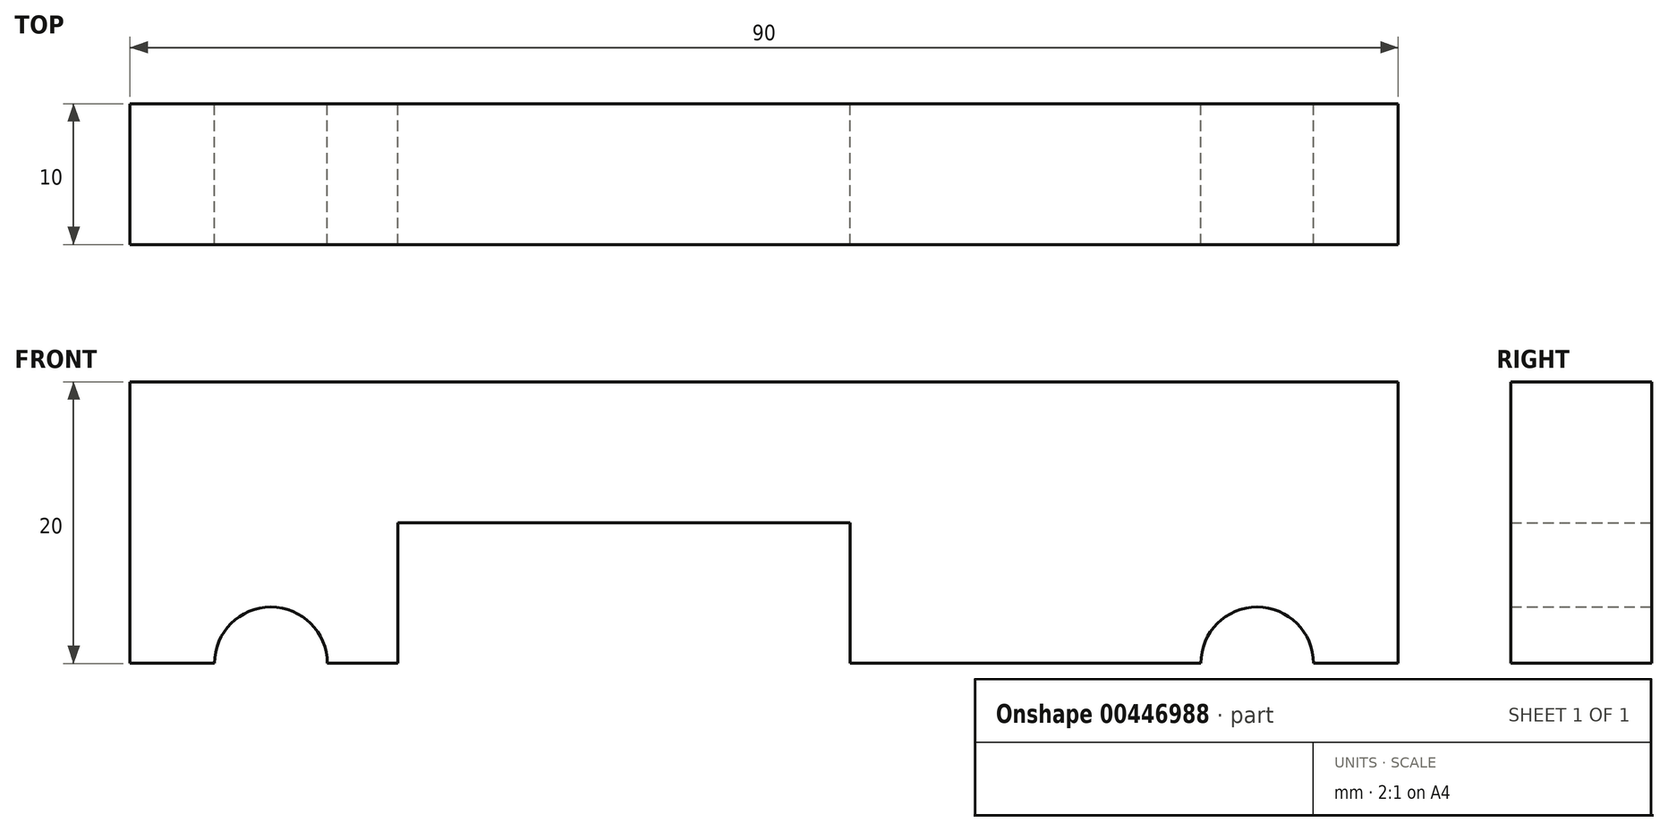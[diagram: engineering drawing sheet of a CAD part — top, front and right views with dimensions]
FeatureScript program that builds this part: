
annotation { "Feature Type Name" : "Feature", "Feature Type Description" : "" }
export const myFeature = defineFeature(function(context is Context, id is Id, definition is map)
    precondition{}
    {
        {
            var Q0;
            Q0=qCreatedBy(makeId("Front.planeOp"),FACE);
            var sketch = newSketch(context, id + "F0", { "sketchPlane" : qUnion([Q0])});
            skLineSegment(sketch, "E0.bottom", {"start": v(-43.64, -19.45) * mm, "end": v(46.36, -19.45) * mm});
            skLineSegment(sketch, "E0.top", {"start": v(-43.64, 0.55) * mm, "end": v(46.36, 0.55) * mm});
            skLineSegment(sketch, "E0.left", {"start": v(-43.64, -19.45) * mm, "end": v(-43.64, 0.55) * mm});
            skLineSegment(sketch, "E0.right", {"start": v(46.36, -19.45) * mm, "end": v(46.36, 0.55) * mm});
            skCircle(sketch, "E1", {"center": v(-33.64, -19.45) * mm, "radius": 4 * mm});
            skCircle(sketch, "E2", {"center": v(36.36, -19.45) * mm, "radius": 4 * mm});
            skLineSegment(sketch, "E3.bottom", {"start": v(-24.64, -19.45) * mm, "end": v(7.46, -19.45) * mm});
            skLineSegment(sketch, "E3.top", {"start": v(-24.64, -9.45) * mm, "end": v(7.46, -9.45) * mm});
            skLineSegment(sketch, "E3.left", {"start": v(-24.64, -19.45) * mm, "end": v(-24.64, -9.45) * mm});
            skLineSegment(sketch, "E3.right", {"start": v(7.46, -19.45) * mm, "end": v(7.46, -9.45) * mm});
            skSolve(sketch);
        }
        {
            var Q0;
            Q0=makeQuery(id+"F0.imprint","IMPRINT",FACE,{"disambiguationData":[TD([[makeQuery(id+"F0.imprint","IMPRINT",EDGE,{"derivedFrom":sQuery(id+"F0.wireOp",EDGE,"E0.top")}),-1.0]])]});
            extrude(context, id + "F1", {"entities" : qUnion([Q0]), "depth" : 10 * mm, "offsetDistance" : 25 * mm});
        }
    });
